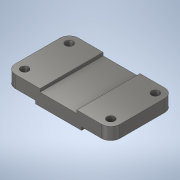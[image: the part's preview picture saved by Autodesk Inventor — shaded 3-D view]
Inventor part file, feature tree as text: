
AUTODESK INVENTOR PART (.ipt)
format: ipt  version: 2020 (Build 240168000, 168)  size: 218,112 bytes
history: native  units: mm
features: extrude x3, sketch x2, fillet x2, mirror x1
ambient origin geometry x8: Origin, YZ Plane, XZ Plane, XY Plane, X Axis, Y Axis, Z Axis, Center Point
bodies: Solid1 (feature_tree)
feature tree (8):
  extrude  "Extrusion1"  Depth=4.0mm
  sketch  "Sketch2"  dims[d2=38.0mm d3=16.0mm d4=44.0mm d5=4.0mm d6=82.0mm d7=0.0mm d8=10.0mm d9=10.0mm d10=12.0mm d11=12.0mm d12=12.0mm d13=12.0mm d14=82.0mm d15=0.0mm d16=82.0mm d17=0.0mm d18=12.0mm d19=12.0mm]
  extrude  "Extrusion2"  Depth=16.0mm
  extrude  "Extrusion3"  Depth=44.0mm
  fillet  "Fillet1"  Radius=4.0mm
  fillet  "Fillet2"  Radius=82.0mm
  mirror  "Mirror1"
  sketch  "Sketch1"  dims[d0=30.0mm d1=4.0mm]
